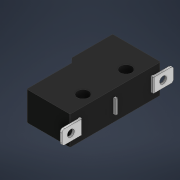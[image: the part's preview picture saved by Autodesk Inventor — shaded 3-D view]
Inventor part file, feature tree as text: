
AUTODESK INVENTOR PART (.ipt)
format: ipt  version: 2022.1 (Build 261234000, 234)  size: 271,872 bytes
history: native  units: mm
features: projected_geometry x8, extrude x7, sketch x7, fillet x6, chamfer x1, direct_edit x1, move_body x1
ambient origin geometry x8: Origin, YZ Plane, XZ Plane, XY Plane, X Axis, Y Axis, Z Axis, Center Point
bodies: Volumenkörper1 (feature_tree)
feature tree (31):
  extrude  "Extrusion1"  Depth=20.0mm
  extrude  "Extrusion2"  Depth=6.35mm TaperAngle=0.0deg
  extrude  "Extrusion3"  Depth=2.0mm
  fillet  "Rundung1"  Radius=2.0mm
  chamfer  "Fase1"  Distance=1.15mm
  fillet  "Rundung2"  Radius=5.0mm
  direct_edit  "Direktbearbeitung1"
  extrude  "Extrusion4"  Depth=0.2mm
  extrude  "Extrusion5"  Depth=0.2mm
  fillet  "Rundung3"  Radius=15.7mm
  fillet  "Rundung4"  Radius=3.1mm
  fillet  "Rundung5"  Radius=16.6mm
  extrude  "Extrusion6"  Depth=0.45mm
  extrude  "Extrusion7"  Depth=0.55mm TaperAngle=0.0deg
  fillet  "Rundung6"  Radius=0.9mm
  sketch  "Skizze1"  dims[d0=10.0mm d1=20.0mm]
  sketch  "Skizze2"  dims[d2=1.0mm d3=6.35mm d4=0.0mm]
  sketch  "Skizze3"  dims[d5=8.15mm d6=2.0mm d7=2.0mm]
  projected_geometry  "Projizierte Kontur1"
  sketch  "Skizze4"  dims[d8=3.43mm d9=1.15mm d10=0.0mm d11=5.0mm]
  projected_geometry  "Projizierte Kontur2"
  sketch  "Skizze5"  dims[d12=0.0mm d13=0.0mm d14=0.2mm]
  projected_geometry  "Projizierte Kontur3"
  projected_geometry  "Projizierte Kontur4"
  sketch  "Skizze6"  dims[d15=1.0mm d16=2.0mm d17=45.0deg d18=0.2mm]
  projected_geometry  "Projizierte Kontur5"
  projected_geometry  "Projizierte Kontur6"
  sketch  "Skizze7"  dims[d19=-0.4mm d20=0.0mm d21=0.0mm d22=15.7mm d23=3.1mm d24=16.6mm d25=0.45mm d26=0.55mm d27=0.0mm d28=0.9mm d29=24.63mm d30=0.55mm d31=0.0mm d32=0.2mm d33=0.1mm d34=0.1mm d35=1.5mm d36=1.5mm d37=10.0mm d38=0.0mm d39=2.5mm d40=12.0mm d41=2.5mm d42=7.0mm d43=1.7mm d44=24.63mm d45=12.315mm d46=2.95mm d47=0.0mm d48=0.0mm d49=0.6mm]
  projected_geometry  "Projizierte Kontur7"
  projected_geometry  "Projizierte Kontur8"
  move_body  "Verschieben1"
